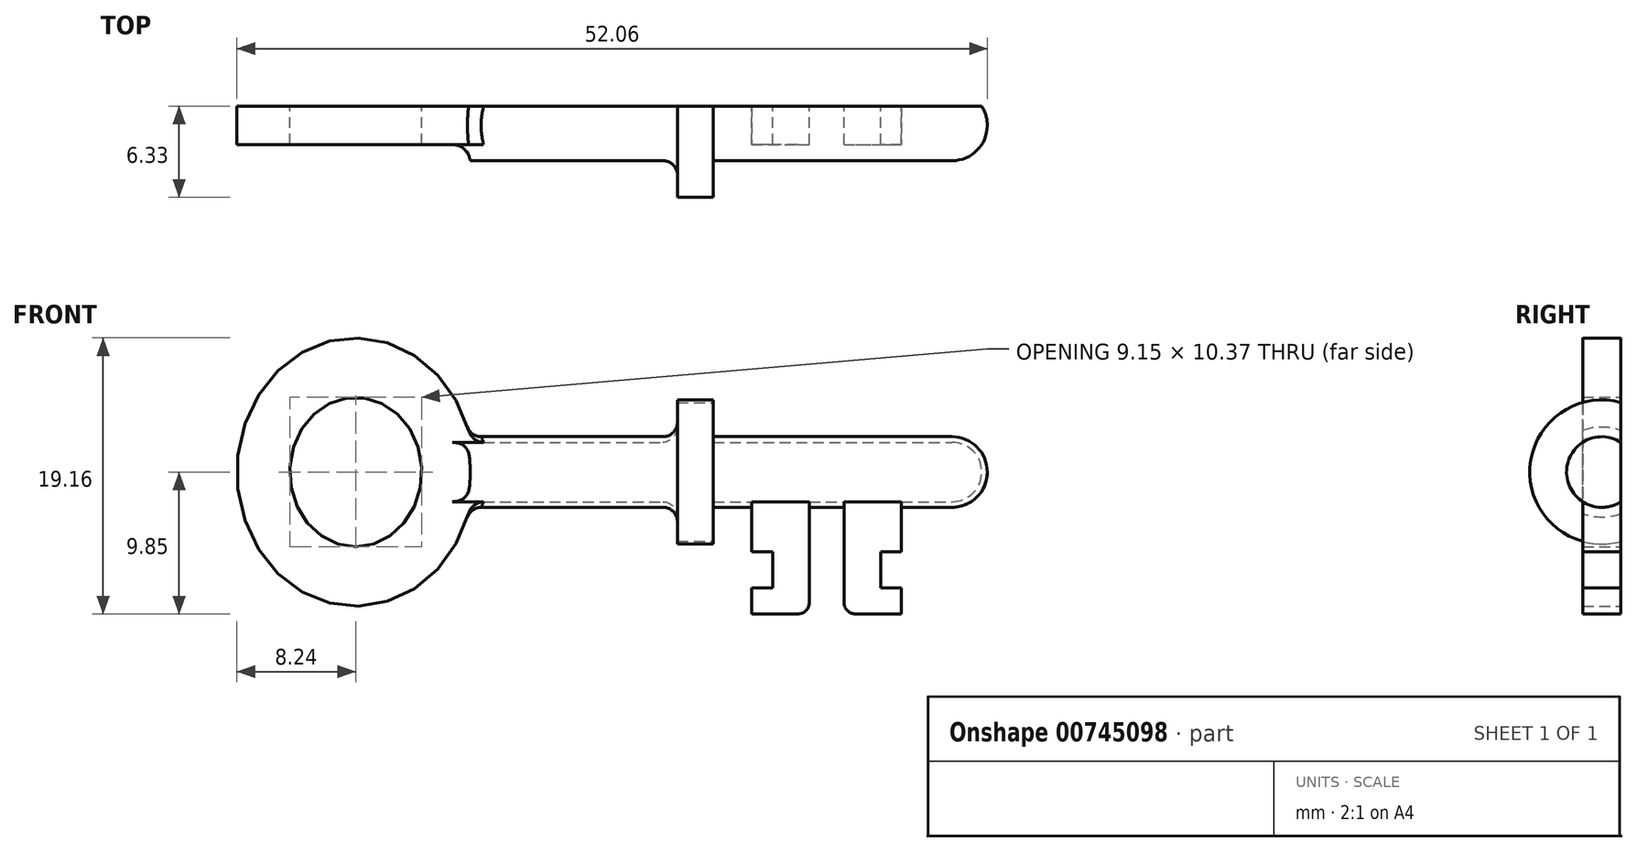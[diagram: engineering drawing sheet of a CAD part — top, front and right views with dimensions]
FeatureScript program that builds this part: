
annotation { "Feature Type Name" : "Feature", "Feature Type Description" : "" }
export const myFeature = defineFeature(function(context is Context, id is Id, definition is map)
    precondition{}
    {
        {
            var Q0;
            Q0=qCreatedBy(makeId("Front.planeOp"),FACE);
            var sketch = newSketch(context, id + "F0", { "sketchPlane" : qUnion([Q0])});
            skLineSegment(sketch, "E0", {"start": v(-24.22, -2.45) * mm, "end": v(-24.22, -9.05) * mm});
            skLineSegment(sketch, "E1", {"start": v(-23.42, -9.85) * mm, "end": v(-20.22, -9.85) * mm});
            skLineSegment(sketch, "E2", {"start": v(-20.22, -9.85) * mm, "end": v(-20.22, -8.05) * mm});
            skLineSegment(sketch, "E3", {"start": v(-20.22, -8.05) * mm, "end": v(-21.67, -8.05) * mm});
            skLineSegment(sketch, "E4", {"start": v(-21.67, -8.05) * mm, "end": v(-21.67, -5.55) * mm});
            skLineSegment(sketch, "E5", {"start": v(-21.67, -5.55) * mm, "end": v(-20.22, -5.55) * mm});
            skLineSegment(sketch, "E6", {"start": v(-20.22, -5.55) * mm, "end": v(-20.22, -2.45) * mm});
            skLineSegment(sketch, "E7", {"start": v(-20.22, -2.45) * mm, "end": v(-24.22, -2.45) * mm});
            skLineSegment(sketch, "E8", {"start": v(-25.42, 28.06) * mm, "end": v(-25.42, -36.4) * mm, "construction": true});
            skLineSegment(sketch, "E9.MirrorCS", {"start": v(-29.17, -5.55) * mm, "end": v(-30.62, -5.55) * mm});
            skLineSegment(sketch, "E10.MirrorCS", {"start": v(-30.62, -9.85) * mm, "end": v(-30.62, -8.05) * mm});
            skLineSegment(sketch, "E11.MirrorCS", {"start": v(-29.17, -8.05) * mm, "end": v(-29.17, -5.55) * mm});
            skLineSegment(sketch, "E12.MirrorCS", {"start": v(-30.62, -8.05) * mm, "end": v(-29.17, -8.05) * mm});
            skLineSegment(sketch, "E13.MirrorCS", {"start": v(-27.42, -9.85) * mm, "end": v(-30.62, -9.85) * mm});
            skLineSegment(sketch, "E14.MirrorCS", {"start": v(-30.62, -2.45) * mm, "end": v(-26.62, -2.45) * mm});
            skLineSegment(sketch, "E15.MirrorCS", {"start": v(-30.62, -5.55) * mm, "end": v(-30.62, -2.45) * mm});
            skLineSegment(sketch, "E16.MirrorCS", {"start": v(-26.62, -2.45) * mm, "end": v(-26.62, -9.05) * mm});
            skLineSegment(sketch, "E17", {"start": v(-20.22, -2.45) * mm, "end": v(-16.72, -2.45) * mm});
            skLineSegment(sketch, "E18", {"start": v(-16.72, -2.45) * mm, "end": v(-16.72, 0) * mm});
            skLineSegment(sketch, "E19", {"start": v(-16.72, 0) * mm, "end": v(-49.85, 0) * mm});
            skLineSegment(sketch, "E20", {"start": v(-50.14, -2.45) * mm, "end": v(-20.22, -2.45) * mm});
            skLineSegment(sketch, "E21.bottom", {"start": v(-35.77, -2.45) * mm, "end": v(-33.27, -2.45) * mm});
            skLineSegment(sketch, "E21.top", {"start": v(-35.77, -5) * mm, "end": v(-33.27, -5) * mm});
            skLineSegment(sketch, "E21.left", {"start": v(-35.77, -2.45) * mm, "end": v(-35.77, -5) * mm});
            skLineSegment(sketch, "E21.right", {"start": v(-33.27, -2.45) * mm, "end": v(-33.27, -5) * mm});
            skPoint(sketch, "E22.visualSharp", {"position": v(-24.22, -9.85) * mm});
            skArc(sketch, "E22.filletArc", {"start": v(-24.22, -9.05) * mm, "mid": v(-23.99, -9.62) * mm, "end": v(-23.42, -9.85) * mm});
            skPoint(sketch, "E23.visualSharp", {"position": v(-26.62, -9.85) * mm});
            skArc(sketch, "E23.filletArc", {"start": v(-27.42, -9.85) * mm, "mid": v(-26.86, -9.62) * mm, "end": v(-26.62, -9.05) * mm});
            skLineSegment(sketch, "E24.top", {"start": v(-30.62, 0) * mm, "end": v(-26.62, 0) * mm});
            skLineSegment(sketch, "E24.left", {"start": v(-30.62, -2.45) * mm, "end": v(-30.62, 0) * mm});
            skLineSegment(sketch, "E24.right", {"start": v(-26.62, -2.45) * mm, "end": v(-26.62, 0) * mm});
            skLineSegment(sketch, "E25.bottom", {"start": v(-24.22, -2.45) * mm, "end": v(-20.22, -2.45) * mm});
            skLineSegment(sketch, "E25.top", {"start": v(-24.22, 0) * mm, "end": v(-20.22, 0) * mm});
            skLineSegment(sketch, "E25.left", {"start": v(-24.22, -2.45) * mm, "end": v(-24.22, 0) * mm});
            skLineSegment(sketch, "E25.right", {"start": v(-20.22, -2.45) * mm, "end": v(-20.22, 0) * mm});
            skArc(sketch, "E26", {"start": v(-16.72, -2.45) * mm, "mid": v(-14.99, -1.73) * mm, "end": v(-14.27, 0) * mm});
            skLineSegment(sketch, "E27", {"start": v(-14.27, 0) * mm, "end": v(-16.72, 0) * mm});
            skEllipse(sketch, "E28", {"center": v(-58.09, 0) * mm, "majorRadius": 9.31 * mm, "minorRadius": 8.24 * mm, "majorAxis": v(0, -1)});
            skEllipse(sketch, "E29", {"center": v(-58.09, 0) * mm, "majorRadius": 5.18 * mm, "minorRadius": 4.58 * mm, "majorAxis": v(0, -1)});
            skSolve(sketch);
        }
        {
            var Q0;
            {var subQ3=sQuery(id+"F0.wireOp",EDGE,"E24.left");Q0=makeQuery(id+"F0.imprint","IMPRINT",FACE,{"disambiguationData":[TD([[makeQuery(id+"F0.imprint","IMPRINT",EDGE,{"derivedFrom":subQ3}),1.0]])]});}
            var Q1;
            Q1=makeQuery(id+"F0.imprint","IMPRINT",FACE,{"disambiguationData":[TD([[makeQuery(id+"F0.imprint","IMPRINT",EDGE,{"derivedFrom":sQuery(id+"F0.wireOp",EDGE,"E21.top")}),1.0]])]});
            var Q2;
            Q2=makeQuery(id+"F0.imprint","IMPRINT",FACE,{"disambiguationData":[TD([[makeQuery(id+"F0.imprint","IMPRINT",EDGE,{"derivedFrom":sQuery(id+"F0.wireOp",EDGE,"E14.MirrorCS")}),1.0]])]});
            var Q3;
            {var subQ0=sQuery(id+"F0.wireOp",EDGE,"E24.right");Q3=makeQuery(id+"F0.imprint","IMPRINT",FACE,{"disambiguationData":[TD([[makeQuery(id+"F0.imprint","IMPRINT",EDGE,{"derivedFrom":subQ0}),-1.0]])]});}
            var Q4;
            Q4=makeQuery(id+"F0.imprint","IMPRINT",FACE,{"disambiguationData":[TD([[makeQuery(id+"F0.imprint","IMPRINT",EDGE,{"derivedFrom":sQuery(id+"F0.wireOp",EDGE,"E7")}),-1.0]])]});
            var Q5;
            Q5=makeQuery(id+"F0.imprint","IMPRINT",FACE,{"disambiguationData":[TD([[makeQuery(id+"F0.imprint","IMPRINT",EDGE,{"derivedFrom":sQuery(id+"F0.wireOp",EDGE,"E17")}),1.0]])]});
            var Q6;
            Q6=makeQuery(id+"F0.imprint","IMPRINT",FACE,{"disambiguationData":[TD([[makeQuery(id+"F0.imprint","IMPRINT",EDGE,{"derivedFrom":sQuery(id+"F0.wireOp",EDGE,"E18")}),-1.0]])]});
            var Q7;
            Q7=sQuery(id+"F0.wireOp",EDGE,"E19");
            revolve(context, id + "F1", {"surfaceOperationType" : NewSurfaceOperationType.NEW, "entities" : qUnion([Q0, Q1, Q2, Q3, Q4, Q5, Q6]), "axis" : qUnion([Q7]), "revolveType" : RevolveType.FULL});
        }
        {
            var Q0;
            Q0=makeQuery(id+"F0.imprint","IMPRINT",FACE,{"disambiguationData":[TD([[makeQuery(id+"F0.imprint","IMPRINT",EDGE,{"derivedFrom":sQuery(id+"F0.wireOp",EDGE,"E9.MirrorCS")}),-1.0]])]});
            var Q1;
            Q1=makeQuery(id+"F0.imprint","IMPRINT",FACE,{"disambiguationData":[TD([[makeQuery(id+"F0.imprint","IMPRINT",EDGE,{"derivedFrom":sQuery(id+"F0.wireOp",EDGE,"E0")}),1.0]])]});
            var Q2;
            Q2=makeQuery(id+"F0.imprint","IMPRINT",FACE,{"disambiguationData":[TD([[makeQuery(id+"F0.imprint","IMPRINT",EDGE,{"derivedFrom":sQuery(id+"F0.wireOp",EDGE,"qf6XsQYD-z7kD-b2Kj-D5VX-HFlL9bcjgPXa")}),-1.0]])]});
            var Q3;
            Q3=makeQuery(id+"F0.imprint","IMPRINT",FACE,{"disambiguationData":[TD([[makeQuery(id+"F0.imprint","IMPRINT",EDGE,{"derivedFrom":sQuery(id+"F0.wireOp",EDGE,"E14.MirrorCS")}),1.0]])]});
            var Q4;
            Q4=makeQuery(id+"F0.imprint","IMPRINT",FACE,{"disambiguationData":[TD([[makeQuery(id+"F0.imprint","IMPRINT",EDGE,{"derivedFrom":sQuery(id+"F0.wireOp",EDGE,"E7")}),-1.0]])]});
            var Q5;
            Q5=makeQuery(id+"F0.imprint","IMPRINT",FACE,{"disambiguationData":[TD([[makeQuery(id+"F0.imprint","IMPRINT",EDGE,{"derivedFrom":sQuery(id+"F0.wireOp",EDGE,"MyRZnK1O-KGg9-q0a5-RYn9-KsevBd75b7iN")}),-1.0]])]});
            var Q6;
            Q6=makeQuery(id+"F0.imprint","IMPRINT",FACE,{"disambiguationData":[TD([[makeQuery(id+"F0.imprint","IMPRINT",EDGE,{"derivedFrom":sQuery(id+"F0.wireOp",EDGE,"TFHr0OS3-0oP0-4jtY-1KdI-hKIv0tCvWhYd")}),-1.0]])]});
            var Q7;
            {var subQ1=sQuery(id+"F0.wireOp",EDGE,"ykkkfEj7-chYN-ZCQU-y8QE-c6QA9kALbc4I");Q7=makeQuery(id+"F0.imprint","IMPRINT",FACE,{"disambiguationData":[TD([[makeQuery(id+"F0.imprint","IMPRINT",EDGE,{"derivedFrom":subQ1}),-1.0]])]});}
            var Q8;
            {var subQ1=sQuery(id+"F0.wireOp",EDGE,"ykkkfEj7-chYN-ZCQU-y8QE-c6QA9kALbc4I");Q8=makeQuery(id+"F0.imprint","IMPRINT",FACE,{"disambiguationData":[TD([[makeQuery(id+"F0.imprint","IMPRINT",EDGE,{"derivedFrom":subQ1}),1.0]])]});}
            var Q9;
            Q9=makeQuery(id+"F0.imprint","IMPRINT",FACE,{"disambiguationData":[TD([[makeQuery(id+"F0.imprint","IMPRINT",EDGE,{"derivedFrom":sQuery(id+"F0.wireOp",EDGE,"Wivs48Q1-gQhC-l1q4-1Sjo-pPSFMFe7QcYe")}),-1.0]])]});
            var Q10;
            Q10=makeQuery(id+"F0.imprint","IMPRINT",FACE,{"disambiguationData":[TD([[makeQuery(id+"F0.imprint","IMPRINT",EDGE,{"derivedFrom":sQuery(id+"F0.wireOp",EDGE,"E29")}),-1.0]])]});
            extrude(context, id + "F2", {"entities" : qUnion([Q0, Q1, Q2, Q3, Q4, Q5, Q6, Q7, Q8, Q9, Q10]), "operationType" : NewBodyOperationType.ADD, "endBound" : BoundingType.SYMMETRIC, "depth" : 2.65 * mm, "offsetDistance" : 25 * mm});
        }
        {
            var Q0;
            Q0=makeQuery(id+"F1.opRevolve","SWEPT_EDGE",EDGE,{"disambiguationData":[OSD([sQuery(id+"F0.wireOp",EDGE,"E20"),sQuery(id+"F0.wireOp",EDGE,"E21.left")])]});
            var Q1;
            {var subQ0=sQuery(id+"F0.wireOp",EDGE,"DqpSNSSK-HpWq-gCTx-igMy-s6QcVx5aDO1A");Q1=makeQuery(id+"F2.boolean.opBoolean","INTERSECT",EDGE,{"derivedFrom":[makeQuery(id+"F1.opRevolve","SWEPT_FACE",FACE,{"disambiguationData":[OSD([subQ0])]}),makeQuery(id+"F2.opExtrude","CAP_FACE",FACE,{"disambiguationData":[OSD([subQ0,sQuery(id+"F0.wireOp",EDGE,"TFHr0OS3-0oP0-4jtY-1KdI-hKIv0tCvWhYd")])],"isStart":true})]});}
            var Q2;
            {var subQ0=sQuery(id+"F0.wireOp",EDGE,"DqpSNSSK-HpWq-gCTx-igMy-s6QcVx5aDO1A");Q2=makeQuery(id+"F2.boolean.opBoolean","INTERSECT",EDGE,{"derivedFrom":[makeQuery(id+"F1.opRevolve","SWEPT_FACE",FACE,{"disambiguationData":[OSD([subQ0])]}),makeQuery(id+"F2.opExtrude","CAP_FACE",FACE,{"disambiguationData":[OSD([subQ0,sQuery(id+"F0.wireOp",EDGE,"TFHr0OS3-0oP0-4jtY-1KdI-hKIv0tCvWhYd")])],"isStart":false})]});}
            var Q3;
            Q3=makeQuery(id+"F2.boolean.opBoolean","INTERSECT",EDGE,{"disambiguationData":[OD(1.0)],"derivedFrom":[makeQuery(id+"F1.opRevolve","SWEPT_FACE",FACE,{"disambiguationData":[OSD([sQuery(id+"F0.wireOp",EDGE,"E20"),sQuery(id+"F0.wireOp",EDGE,"3AQQNRzy-mWYm-i2UZ-XKw3-H57PDRYjsVSW")])]}),makeQuery(id+"F2.opExtrude","SWEPT_FACE",FACE,{"disambiguationData":[OSD([sQuery(id+"F0.wireOp",EDGE,"DqpSNSSK-HpWq-gCTx-igMy-s6QcVx5aDO1A")])]})]});
            var Q4;
            Q4=makeQuery(id+"F2.boolean.opBoolean","INTERSECT",EDGE,{"disambiguationData":[OD(0.0)],"derivedFrom":[makeQuery(id+"F1.opRevolve","SWEPT_FACE",FACE,{"disambiguationData":[OSD([sQuery(id+"F0.wireOp",EDGE,"E20"),sQuery(id+"F0.wireOp",EDGE,"3AQQNRzy-mWYm-i2UZ-XKw3-H57PDRYjsVSW")])]}),makeQuery(id+"F2.opExtrude","SWEPT_FACE",FACE,{"disambiguationData":[OSD([sQuery(id+"F0.wireOp",EDGE,"DqpSNSSK-HpWq-gCTx-igMy-s6QcVx5aDO1A")])]})]});
            var Q5;
            {var subQ0=sQuery(id+"F0.wireOp",EDGE,"E28");Q5=makeQuery(id+"F2.boolean.opBoolean","INTERSECT",EDGE,{"derivedFrom":[makeQuery(id+"F1.opRevolve","SWEPT_FACE",FACE,{"disambiguationData":[OSD([subQ0])]}),makeQuery(id+"F2.opExtrude","CAP_FACE",FACE,{"disambiguationData":[OSD([subQ0,sQuery(id+"F0.wireOp",EDGE,"E29")])],"isStart":false})]});}
            var Q6;
            {var subQ0=sQuery(id+"F0.wireOp",EDGE,"E28");Q6=makeQuery(id+"F2.boolean.opBoolean","INTERSECT",EDGE,{"derivedFrom":[makeQuery(id+"F1.opRevolve","SWEPT_FACE",FACE,{"disambiguationData":[OSD([subQ0])]}),makeQuery(id+"F2.opExtrude","CAP_FACE",FACE,{"disambiguationData":[OSD([subQ0,sQuery(id+"F0.wireOp",EDGE,"E29")])],"isStart":true})]});}
            var Q7;
            Q7=makeQuery(id+"F2.boolean.opBoolean","INTERSECT",EDGE,{"disambiguationData":[OD(1.0)],"derivedFrom":[makeQuery(id+"F1.opRevolve","SWEPT_FACE",FACE,{"disambiguationData":[OSD([sQuery(id+"F0.wireOp",EDGE,"E20")])]}),makeQuery(id+"F2.opExtrude","SWEPT_FACE",FACE,{"disambiguationData":[OSD([sQuery(id+"F0.wireOp",EDGE,"E28")])]})]});
            var Q8;
            Q8=makeQuery(id+"F2.boolean.opBoolean","INTERSECT",EDGE,{"disambiguationData":[OD(0.0)],"derivedFrom":[makeQuery(id+"F1.opRevolve","SWEPT_FACE",FACE,{"disambiguationData":[OSD([sQuery(id+"F0.wireOp",EDGE,"E20")])]}),makeQuery(id+"F2.opExtrude","SWEPT_FACE",FACE,{"disambiguationData":[OSD([sQuery(id+"F0.wireOp",EDGE,"E28")])]})]});
            fillet(context, id + "F3", {"entities" : qUnion([Q0, Q1, Q2, Q3, Q4, Q5, Q6, Q7, Q8]), "radius" : 1 * mm, "tangentPropagation" : true, "allowEdgeOverflow" : false});
        }
        {
            var Q0;
            Q0=makeQuery(id+"F2.opExtrude","SWEPT_FACE",FACE,{"disambiguationData":[OSD([sQuery(id+"F0.wireOp",EDGE,"E13.MirrorCS")])]});
            var sketch = newSketch(context, id + "F4", { "sketchPlane" : qUnion([Q0])});
            skLineSegment(sketch, "E30.0", {"start": v(-27.42, -1.32) * mm, "end": v(-30.62, -1.32) * mm});
            skLineSegment(sketch, "E31.0", {"start": v(-27.42, 1.32) * mm, "end": v(-30.62, 1.32) * mm});
            skLineSegment(sketch, "E32.bottom", {"start": v(-9.48, 1.32) * mm, "end": v(-65.17, 1.32) * mm});
            skLineSegment(sketch, "E32.top", {"start": v(-9.48, 4.9) * mm, "end": v(-65.17, 4.9) * mm});
            skLineSegment(sketch, "E32.left", {"start": v(-9.48, 1.32) * mm, "end": v(-9.48, 4.9) * mm});
            skLineSegment(sketch, "E32.right", {"start": v(-65.17, 1.32) * mm, "end": v(-65.17, 4.9) * mm});
            skLineSegment(sketch, "E33.bottom", {"start": v(-9.48, -1.33) * mm, "end": v(-65.17, -1.33) * mm});
            skLineSegment(sketch, "E33.top", {"start": v(-9.48, -6.11) * mm, "end": v(-65.17, -6.11) * mm});
            skLineSegment(sketch, "E33.left", {"start": v(-9.48, -1.33) * mm, "end": v(-9.48, -6.11) * mm});
            skLineSegment(sketch, "E33.right", {"start": v(-65.17, -1.33) * mm, "end": v(-65.17, -6.11) * mm});
            skSolve(sketch);
        }
        {
            var Q0;
            Q0=makeQuery(id+"F4.imprint","IMPRINT",FACE,{"disambiguationData":[TD([[makeQuery(id+"F4.imprint","IMPRINT",EDGE,{"derivedFrom":sQuery(id+"F4.wireOp",EDGE,"E33.top")}),-1.0]])]});
            extrude(context, id + "F5", {"entities" : qUnion([Q0]), "operationType" : NewBodyOperationType.REMOVE, "endBound" : BoundingType.THROUGH_ALL, "oppositeDirection" : true, "depth" : 25 * mm, "offsetDistance" : 25 * mm});
        }
    });
